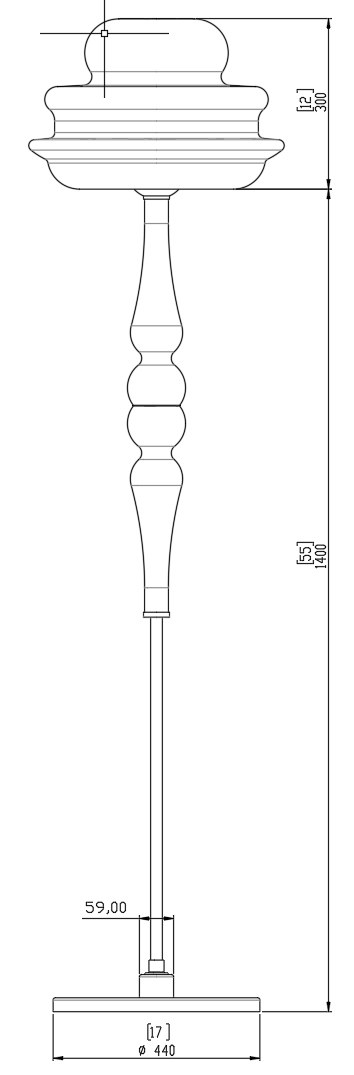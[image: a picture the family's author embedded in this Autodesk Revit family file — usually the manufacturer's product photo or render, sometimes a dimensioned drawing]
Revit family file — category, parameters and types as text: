
# Revit family: NOVECENTO-Suspension
name_source: partatom
category: Lighting Fixtures
units: mm (PartAtom-declared; Revit-internal decimal feet)

## family parameters
Always vertical = Yes
Cut with Voids When Loaded = No
Host = Ceiling
Light Source = No
OmniClass Number = 23.80.70.11
OmniClass Title = Luminaries for Internal Lighting
Part Type = Normal
Room Calculation Point = No
Round Connector Dimension = Use Diameter
Shared = No

## types (3) — shared parameters
Bulb Diametr = 15 mm  [stored 0.0492126 ft]
Country = Europe
Description = SUSPENSION
Designer = Studio Debonademeo
Manufacturer = Vistosi
Manufacturer country = Italy
Model = NOVECENTO
Type Comments = Studio Debonademeo
URL = https://vistosi.com
URL Product Page = https://vistosi.it
zero-valued in all types: Default Elevation, Depth

## per-type parameters (varying)
| type | Lampshade Type | SP M and SP G | SP P | Width |
| NOVECENTO SP G | NOVECENTO_Lampshade : Novecento SP G | Yes | No | 64 mm |
| NOVECENTO SP P | NOVECENTO_Lampshade : Novecento SP P | No | Yes | 27 mm |
| NOVECENTO SP M | NOVECENTO_Lampshade : Novecento SP M | Yes | No | 44 mm |

note: [stored X ft] marks values corroborated as IEEE doubles in the binary element streams (Revit-internal decimal feet)

## geometry (parser evidence)
native form markers: Sweep x17
no freeform markers — native parametric forms only
